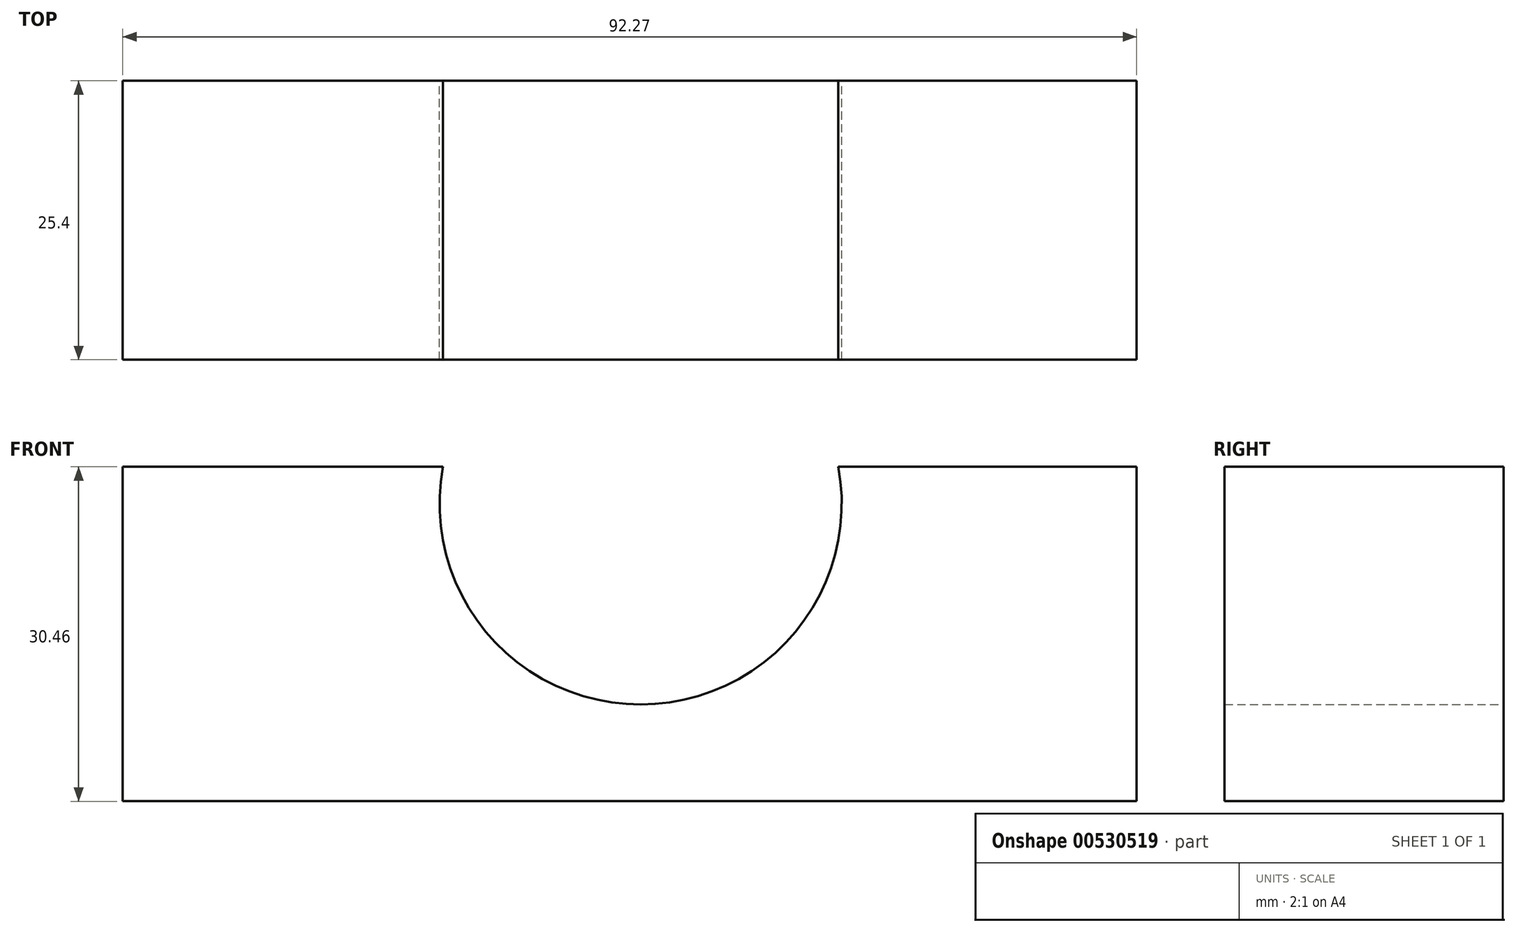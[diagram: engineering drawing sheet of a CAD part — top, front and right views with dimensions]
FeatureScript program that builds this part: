
annotation { "Feature Type Name" : "Feature", "Feature Type Description" : "" }
export const myFeature = defineFeature(function(context is Context, id is Id, definition is map)
    precondition{}
    {
        {
            var Q0;
            Q0=qCreatedBy(makeId("Front.planeOp"),FACE);
            var sketch = newSketch(context, id + "F0", { "sketchPlane" : qUnion([Q0])});
            skLineSegment(sketch, "E0", {"start": v(-55.79, -30.46) * mm, "end": v(36.69, -30.46) * mm});
            skLineSegment(sketch, "E1", {"start": v(36.69, -30.46) * mm, "end": v(36.69, 0) * mm});
            skLineSegment(sketch, "E2", {"start": v(36.69, 0) * mm, "end": v(-55.58, 0) * mm});
            skLineSegment(sketch, "E3", {"start": v(-55.58, 0) * mm, "end": v(-55.58, -32.06) * mm});
            skArc(sketch, "E4", {"start": v(-26.44, 0) * mm, "mid": v(-6.4, -21.53) * mm, "end": v(8.34, 3.92) * mm});
            skSolve(sketch);
        }
        {
            var Q0;
            {var subQ5=sQuery(id+"F0.wireOp",EDGE,"E1");Q0=makeQuery(id+"F0.imprint","IMPRINT",FACE,{"disambiguationData":[TD([[makeQuery(id+"F0.imprint","IMPRINT",EDGE,{"derivedFrom":subQ5}),1.0]])]});}
            extrude(context, id + "F1", {"entities" : qUnion([Q0]), "depth" : 25.4 * mm, "offsetDistance" : 25.4 * mm});
        }
    });
